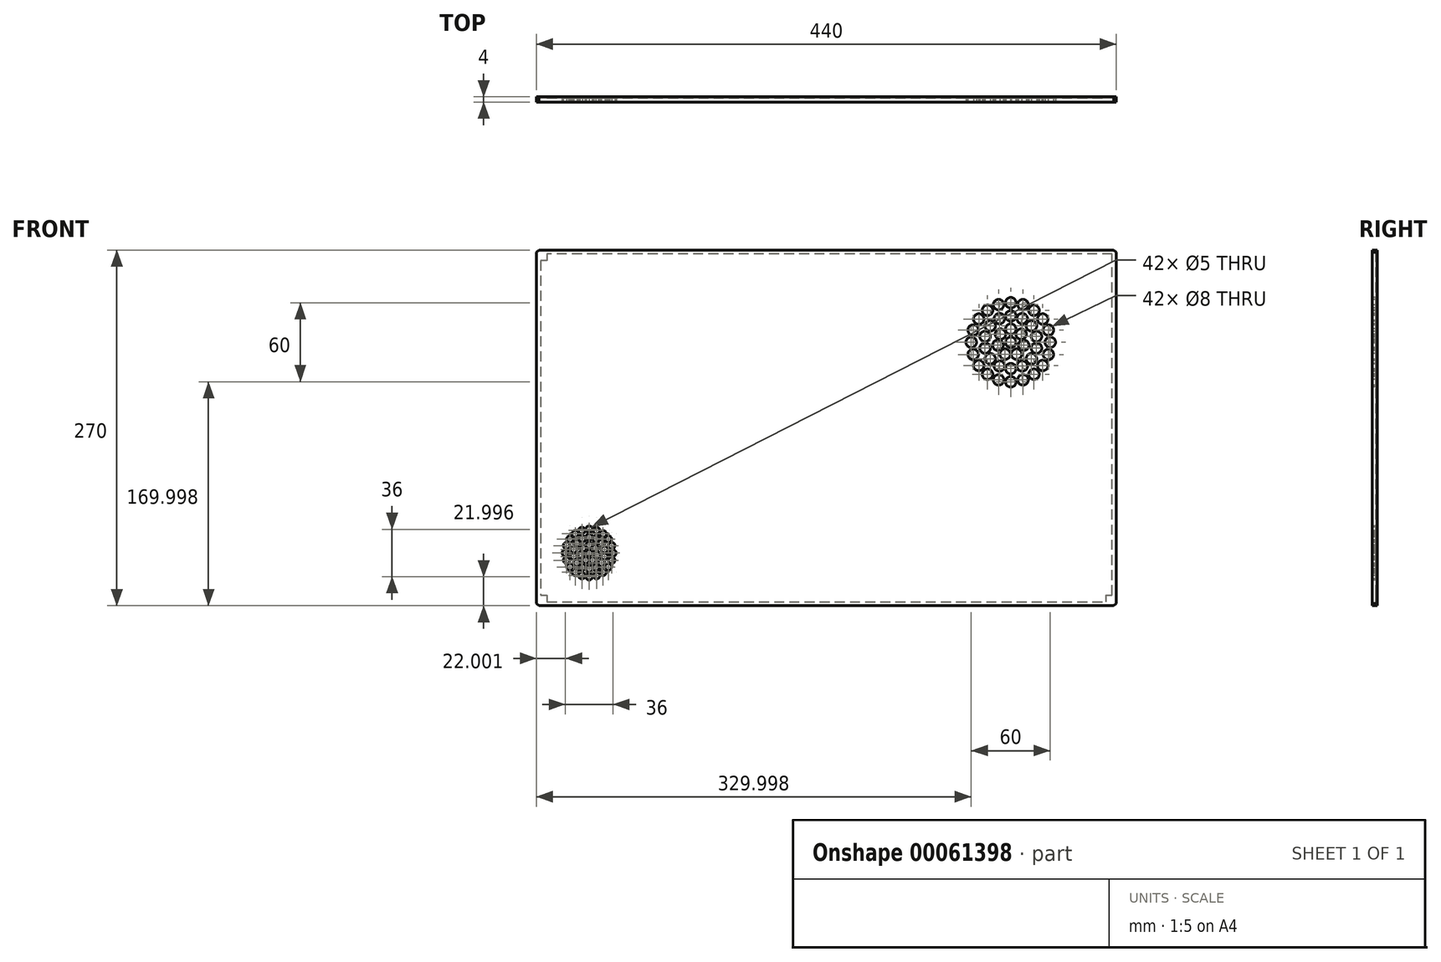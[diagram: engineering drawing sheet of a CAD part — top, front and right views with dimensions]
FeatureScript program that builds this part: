
annotation { "Feature Type Name" : "Feature", "Feature Type Description" : "" }
export const myFeature = defineFeature(function(context is Context, id is Id, definition is map)
    precondition{}
    {
        {
            var Q0;
            Q0=qCreatedBy(makeId("Front.planeOp"),FACE);
            var sketch = newSketch(context, id + "F0", { "sketchPlane" : qUnion([Q0])});
            skLineSegment(sketch, "E0", {"start": v(217.23, 153.99) * mm, "end": v(-222.77, 153.99) * mm});
            skLineSegment(sketch, "E1", {"start": v(-222.77, 153.99) * mm, "end": v(-222.77, -116.01) * mm});
            skLineSegment(sketch, "E2", {"start": v(-222.77, -116.01) * mm, "end": v(217.23, -116.01) * mm});
            skLineSegment(sketch, "E3", {"start": v(217.23, -116.01) * mm, "end": v(217.23, 153.99) * mm});
            skSolve(sketch);
        }
        {
            var Q0;
            Q0 = qSketchRegion(id + "F0", true);
            extrude(context, id + "F1", {"entities" : qUnion([Q0]), "depth" : 4 * mm});
        }
        {
            var Q0;
            Q0=makeQuery(id+"F1.opExtrude","CAP_FACE",FACE,{"disambiguationData":[OSD([sQuery(id+"F0.wireOp",EDGE,"E0"),sQuery(id+"F0.wireOp",EDGE,"3un7jIAZ-FrQ3-j853-8rkc-LdJFk3uyKHBQ"),sQuery(id+"F0.wireOp",EDGE,"E1"),sQuery(id+"F0.wireOp",EDGE,"AtWhbvsI-1UGR-Bnte-KNUE-ymeLdUukXcOe"),sQuery(id+"F0.wireOp",EDGE,"E2"),sQuery(id+"F0.wireOp",EDGE,"B4eVaFRD-0TVU-WoEL-3ROC-KdzaxgXNt1TW"),sQuery(id+"F0.wireOp",EDGE,"E3"),sQuery(id+"F0.wireOp",EDGE,"RKecPICw-fRl2-04lv-uSGy-0Mqtrs9AMaEl")])],"isStart":true});
            shell(context, id + "F2", {"entities" : qUnion([Q0]), "thickness" : 3 * mm});
        }
        {
            var Q0;
            Q0=makeQuery(id+"F2.opShell","OFFSET_FACE",FACE,{"disambiguationData":[OSD([sQuery(id+"F0.wireOp",EDGE,"E0"),sQuery(id+"F0.wireOp",EDGE,"3un7jIAZ-FrQ3-j853-8rkc-LdJFk3uyKHBQ"),sQuery(id+"F0.wireOp",EDGE,"E1"),sQuery(id+"F0.wireOp",EDGE,"AtWhbvsI-1UGR-Bnte-KNUE-ymeLdUukXcOe"),sQuery(id+"F0.wireOp",EDGE,"E2"),sQuery(id+"F0.wireOp",EDGE,"B4eVaFRD-0TVU-WoEL-3ROC-KdzaxgXNt1TW"),sQuery(id+"F0.wireOp",EDGE,"E3"),sQuery(id+"F0.wireOp",EDGE,"RKecPICw-fRl2-04lv-uSGy-0Mqtrs9AMaEl")])]});
            var sketch = newSketch(context, id + "F3", { "sketchPlane" : qUnion([Q0])});
            skLineSegment(sketch, "E4.bottom", {"start": v(214.77, -113.01) * mm, "end": v(219.77, -113.01) * mm});
            skLineSegment(sketch, "E4.top", {"start": v(214.77, -108.01) * mm, "end": v(219.77, -108.01) * mm});
            skLineSegment(sketch, "E4.left", {"start": v(219.77, -113.01) * mm, "end": v(219.77, -108.01) * mm});
            skLineSegment(sketch, "E4.right", {"start": v(214.77, -113.01) * mm, "end": v(214.77, -108.01) * mm});
            skLineSegment(sketch, "E5.bottom", {"start": v(219.77, 150.99) * mm, "end": v(214.77, 150.99) * mm});
            skLineSegment(sketch, "E5.top", {"start": v(219.77, 145.99) * mm, "end": v(214.77, 145.99) * mm});
            skLineSegment(sketch, "E5.left", {"start": v(219.77, 145.99) * mm, "end": v(219.77, 150.99) * mm});
            skLineSegment(sketch, "E5.right", {"start": v(214.77, 145.99) * mm, "end": v(214.77, 150.99) * mm});
            skLineSegment(sketch, "E6.bottom", {"start": v(-214.23, -113.01) * mm, "end": v(-209.23, -113.01) * mm});
            skLineSegment(sketch, "E6.top", {"start": v(-214.23, -108.01) * mm, "end": v(-209.23, -108.01) * mm});
            skLineSegment(sketch, "E6.left", {"start": v(-214.23, -113.01) * mm, "end": v(-214.23, -108.01) * mm});
            skLineSegment(sketch, "E6.right", {"start": v(-209.23, -113.01) * mm, "end": v(-209.23, -108.01) * mm});
            skSolve(sketch);
        }
        {
            var Q0;
            Q0=makeQuery(id+"F1.opExtrude","SWEPT_EDGE",EDGE,{"disambiguationData":[OSD([sQuery(id+"F0.wireOp",EDGE,"E1"),sQuery(id+"F0.wireOp",EDGE,"E2")])]});
            var Q1;
            Q1=makeQuery(id+"F1.opExtrude","SWEPT_EDGE",EDGE,{"disambiguationData":[OSD([sQuery(id+"F0.wireOp",EDGE,"E0"),sQuery(id+"F0.wireOp",EDGE,"E1")])]});
            var Q2;
            Q2=makeQuery(id+"F1.opExtrude","SWEPT_EDGE",EDGE,{"disambiguationData":[OSD([sQuery(id+"F0.wireOp",EDGE,"E0"),sQuery(id+"F0.wireOp",EDGE,"E3")])]});
            var Q3;
            Q3=makeQuery(id+"F1.opExtrude","SWEPT_EDGE",EDGE,{"disambiguationData":[OSD([sQuery(id+"F0.wireOp",EDGE,"E2"),sQuery(id+"F0.wireOp",EDGE,"E3")])]});
            chamfer(context, id + "F4", {"entities" : qUnion([Q0, Q1, Q2, Q3]), "width" : 1.78 * mm, "tangentPropagation" : true});
        }
        {
            var Q0;
            Q0 = qSketchRegion(id + "F3", true);
            var Q1;
            Q1=makeQuery(id+"F1.opExtrude","CAP_FACE",FACE,{"disambiguationData":[OSD([sQuery(id+"F0.wireOp",EDGE,"E0"),sQuery(id+"F0.wireOp",EDGE,"E1"),sQuery(id+"F0.wireOp",EDGE,"E2"),sQuery(id+"F0.wireOp",EDGE,"E3")])],"isStart":true});
            extrude(context, id + "F5", {"entities" : qUnion([Q0]), "operationType" : NewBodyOperationType.ADD, "endBound" : BoundingType.UP_TO_SURFACE, "endBoundEntityFace" : qUnion([Q1]), "depth" : 25 * mm});
        }
        {
            var Q0;
            Q0=makeQuery(id+"F1.opExtrude","CAP_FACE",FACE,{"disambiguationData":[OSD([sQuery(id+"F0.wireOp",EDGE,"E0"),sQuery(id+"F0.wireOp",EDGE,"E1"),sQuery(id+"F0.wireOp",EDGE,"E2"),sQuery(id+"F0.wireOp",EDGE,"E3")])],"isStart":false});
            var sketch = newSketch(context, id + "F6", { "sketchPlane" : qUnion([Q0])});
            skPoint(sketch, "E7", {"position": v(-182.77, -116.01) * mm});
            skPoint(sketch, "E8", {"position": v(-222.77, -10.4) * mm});
            skPoint(sketch, "E9", {"position": v(-182.77, -76.01) * mm});
            skCircle(sketch, "E10", {"center": v(-182.77, -58.01) * mm, "radius": 2.5 * mm});
            skCircle(sketch, "E11.1.0", {"center": v(-188.33, -58.9) * mm, "radius": 2.5 * mm});
            skCircle(sketch, "E11.2.0", {"center": v(-193.35, -61.45) * mm, "radius": 2.5 * mm});
            skCircle(sketch, "E12.1.3.0", {"center": v(-197.33, -65.43) * mm, "radius": 2.5 * mm});
            skCircle(sketch, "E12.1.4.0", {"center": v(-199.89, -70.45) * mm, "radius": 2.5 * mm});
            skCircle(sketch, "E12.1.5.0", {"center": v(-200.77, -76.01) * mm, "radius": 2.5 * mm});
            skCircle(sketch, "E12.1.6.0", {"center": v(-199.89, -81.58) * mm, "radius": 2.5 * mm});
            skCircle(sketch, "E12.1.7.0", {"center": v(-197.33, -86.6) * mm, "radius": 2.5 * mm});
            skCircle(sketch, "E12.1.8.0", {"center": v(-193.35, -90.58) * mm, "radius": 2.5 * mm});
            skCircle(sketch, "E13.1.9.0", {"center": v(-188.33, -93.13) * mm, "radius": 2.5 * mm});
            skCircle(sketch, "E13.1.10.0", {"center": v(-182.77, -94.01) * mm, "radius": 2.5 * mm});
            skCircle(sketch, "E13.1.11.0", {"center": v(-177.2, -93.13) * mm, "radius": 2.5 * mm});
            skCircle(sketch, "E14.1.12.0", {"center": v(-172.19, -90.58) * mm, "radius": 2.5 * mm});
            skCircle(sketch, "E14.1.13.0", {"center": v(-168.2, -86.6) * mm, "radius": 2.5 * mm});
            skCircle(sketch, "E15", {"center": v(-182.77, -64.01) * mm, "radius": 2.5 * mm});
            skCircle(sketch, "E16.1.0", {"center": v(-187.98, -65.2) * mm, "radius": 2.5 * mm});
            skCircle(sketch, "E16.2.0", {"center": v(-192.15, -68.53) * mm, "radius": 2.5 * mm});
            skCircle(sketch, "E16.3.0", {"center": v(-194.47, -73.34) * mm, "radius": 2.5 * mm});
            skCircle(sketch, "E16.4.0", {"center": v(-194.47, -78.68) * mm, "radius": 2.5 * mm});
            skCircle(sketch, "E16.5.0", {"center": v(-192.15, -83.5) * mm, "radius": 2.5 * mm});
            skCircle(sketch, "E16.6.0", {"center": v(-187.98, -86.83) * mm, "radius": 2.5 * mm});
            skCircle(sketch, "E17.1.7.0", {"center": v(-182.77, -88.01) * mm, "radius": 2.5 * mm});
            skCircle(sketch, "E17.1.8.0", {"center": v(-177.56, -86.83) * mm, "radius": 2.5 * mm});
            skCircle(sketch, "E17.1.9.0", {"center": v(-173.39, -83.5) * mm, "radius": 2.5 * mm});
            skCircle(sketch, "E18", {"center": v(-182.77, -70.01) * mm, "radius": 2.5 * mm});
            skCircle(sketch, "E19.1.0", {"center": v(-187.46, -72.27) * mm, "radius": 2.5 * mm});
            skCircle(sketch, "E19.2.0", {"center": v(-188.62, -77.35) * mm, "radius": 2.5 * mm});
            skCircle(sketch, "E19.3.0", {"center": v(-185.37, -81.42) * mm, "radius": 2.5 * mm});
            skCircle(sketch, "E19.4.0", {"center": v(-180.17, -81.42) * mm, "radius": 2.5 * mm});
            skCircle(sketch, "E19.5.0", {"center": v(-176.92, -77.35) * mm, "radius": 2.5 * mm});
            skCircle(sketch, "E19.6.0", {"center": v(-178.08, -72.27) * mm, "radius": 2.5 * mm});
            skCircle(sketch, "E20", {"center": v(-182.77, -76.01) * mm, "radius": 2.5 * mm});
            skCircle(sketch, "E21.1.14.0", {"center": v(-165.65, -81.58) * mm, "radius": 2.5 * mm});
            skCircle(sketch, "E21.1.15.0", {"center": v(-164.77, -76.01) * mm, "radius": 2.5 * mm});
            skCircle(sketch, "E21.1.16.0", {"center": v(-165.65, -70.45) * mm, "radius": 2.5 * mm});
            skCircle(sketch, "E22.1.10.0", {"center": v(-171.07, -78.68) * mm, "radius": 2.5 * mm});
            skCircle(sketch, "E22.1.11.0", {"center": v(-171.07, -73.34) * mm, "radius": 2.5 * mm});
            skCircle(sketch, "E23.1.17.0", {"center": v(-168.2, -65.43) * mm, "radius": 2.5 * mm});
            skCircle(sketch, "E23.1.18.0", {"center": v(-172.19, -61.45) * mm, "radius": 2.5 * mm});
            skCircle(sketch, "E23.1.19.0", {"center": v(-177.2, -58.9) * mm, "radius": 2.5 * mm});
            skCircle(sketch, "E24.1.12.0", {"center": v(-173.39, -68.53) * mm, "radius": 2.5 * mm});
            skCircle(sketch, "E24.1.13.0", {"center": v(-177.56, -65.2) * mm, "radius": 2.5 * mm});
            skSolve(sketch);
        }
        {
            var Q0;
            Q0 = qSketchRegion(id + "F6", true);
            extrude(context, id + "F7", {"entities" : qUnion([Q0]), "operationType" : NewBodyOperationType.REMOVE, "endBound" : BoundingType.THROUGH_ALL, "oppositeDirection" : true, "depth" : 25 * mm});
        }
        {
            var Q0;
            Q0=makeQuery(id+"F1.opExtrude","CAP_FACE",FACE,{"disambiguationData":[OSD([sQuery(id+"F0.wireOp",EDGE,"E0"),sQuery(id+"F0.wireOp",EDGE,"E1"),sQuery(id+"F0.wireOp",EDGE,"E2"),sQuery(id+"F0.wireOp",EDGE,"E3")])],"isStart":false});
            var sketch = newSketch(context, id + "F8", { "sketchPlane" : qUnion([Q0])});
            skPoint(sketch, "E25", {"position": v(137.23, 83.99) * mm});
            skCircle(sketch, "E26", {"center": v(137.23, 113.99) * mm, "radius": 4 * mm});
            skCircle(sketch, "E27.1.0", {"center": v(127.96, 112.52) * mm, "radius": 4 * mm});
            skCircle(sketch, "E27.2.0", {"center": v(119.6, 108.26) * mm, "radius": 4 * mm});
            skCircle(sketch, "E28.1.3.0", {"center": v(112.96, 101.62) * mm, "radius": 4 * mm});
            skCircle(sketch, "E28.1.4.0", {"center": v(108.7, 93.26) * mm, "radius": 4 * mm});
            skCircle(sketch, "E28.1.5.0", {"center": v(107.23, 83.99) * mm, "radius": 4 * mm});
            skCircle(sketch, "E28.1.6.0", {"center": v(108.7, 74.72) * mm, "radius": 4 * mm});
            skCircle(sketch, "E28.1.7.0", {"center": v(112.96, 66.35) * mm, "radius": 4 * mm});
            skCircle(sketch, "E28.1.8.0", {"center": v(119.6, 59.72) * mm, "radius": 4 * mm});
            skCircle(sketch, "E29.1.9.0", {"center": v(127.96, 55.46) * mm, "radius": 4 * mm});
            skCircle(sketch, "E29.1.10.0", {"center": v(137.23, 53.99) * mm, "radius": 4 * mm});
            skCircle(sketch, "E29.1.11.0", {"center": v(146.5, 55.46) * mm, "radius": 4 * mm});
            skCircle(sketch, "E30.1.12.0", {"center": v(154.86, 59.72) * mm, "radius": 4 * mm});
            skCircle(sketch, "E30.1.13.0", {"center": v(161.5, 66.35) * mm, "radius": 4 * mm});
            skCircle(sketch, "E31", {"center": v(137.23, 103.99) * mm, "radius": 4 * mm});
            skCircle(sketch, "E32.1.0", {"center": v(128.55, 102) * mm, "radius": 4 * mm});
            skCircle(sketch, "E32.2.0", {"center": v(121.6, 96.46) * mm, "radius": 4 * mm});
            skCircle(sketch, "E32.3.0", {"center": v(117.73, 88.44) * mm, "radius": 4 * mm});
            skCircle(sketch, "E32.4.0", {"center": v(117.73, 79.54) * mm, "radius": 4 * mm});
            skCircle(sketch, "E32.5.0", {"center": v(121.6, 71.52) * mm, "radius": 4 * mm});
            skCircle(sketch, "E32.6.0", {"center": v(128.55, 65.97) * mm, "radius": 4 * mm});
            skCircle(sketch, "E33.1.7.0", {"center": v(137.23, 63.99) * mm, "radius": 4 * mm});
            skCircle(sketch, "E33.1.8.0", {"center": v(145.9, 65.97) * mm, "radius": 4 * mm});
            skCircle(sketch, "E33.1.9.0", {"center": v(152.86, 71.52) * mm, "radius": 4 * mm});
            skCircle(sketch, "E34", {"center": v(137.23, 93.99) * mm, "radius": 4 * mm});
            skCircle(sketch, "E35.1.0", {"center": v(129.4, 90.22) * mm, "radius": 4 * mm});
            skCircle(sketch, "E35.2.0", {"center": v(127.48, 81.76) * mm, "radius": 4 * mm});
            skCircle(sketch, "E35.3.0", {"center": v(132.89, 74.98) * mm, "radius": 4 * mm});
            skCircle(sketch, "E35.4.0", {"center": v(141.57, 74.98) * mm, "radius": 4 * mm});
            skCircle(sketch, "E35.5.0", {"center": v(146.98, 81.76) * mm, "radius": 4 * mm});
            skCircle(sketch, "E35.6.0", {"center": v(145.05, 90.22) * mm, "radius": 4 * mm});
            skCircle(sketch, "E36", {"center": v(137.23, 83.99) * mm, "radius": 4 * mm});
            skCircle(sketch, "E37.1.14.0", {"center": v(165.76, 74.72) * mm, "radius": 4 * mm});
            skCircle(sketch, "E37.1.15.0", {"center": v(167.23, 83.99) * mm, "radius": 4 * mm});
            skCircle(sketch, "E37.1.16.0", {"center": v(165.76, 93.26) * mm, "radius": 4 * mm});
            skCircle(sketch, "E38.1.10.0", {"center": v(156.73, 79.54) * mm, "radius": 4 * mm});
            skCircle(sketch, "E38.1.11.0", {"center": v(156.73, 88.44) * mm, "radius": 4 * mm});
            skCircle(sketch, "E39.1.17.0", {"center": v(161.5, 101.62) * mm, "radius": 4 * mm});
            skCircle(sketch, "E39.1.18.0", {"center": v(154.86, 108.26) * mm, "radius": 4 * mm});
            skCircle(sketch, "E39.1.19.0", {"center": v(146.5, 112.52) * mm, "radius": 4 * mm});
            skCircle(sketch, "E40.1.12.0", {"center": v(152.86, 96.46) * mm, "radius": 4 * mm});
            skCircle(sketch, "E40.1.13.0", {"center": v(145.9, 102) * mm, "radius": 4 * mm});
            skPoint(sketch, "E41", {"position": v(137.23, 153.99) * mm});
            skPoint(sketch, "E42", {"position": v(217.23, 83.99) * mm});
            skSolve(sketch);
        }
        {
            var Q0;
            Q0 = qSketchRegion(id + "F8", true);
            extrude(context, id + "F9", {"entities" : qUnion([Q0]), "operationType" : NewBodyOperationType.REMOVE, "endBound" : BoundingType.THROUGH_ALL, "oppositeDirection" : true, "depth" : 25 * mm});
        }
    });
